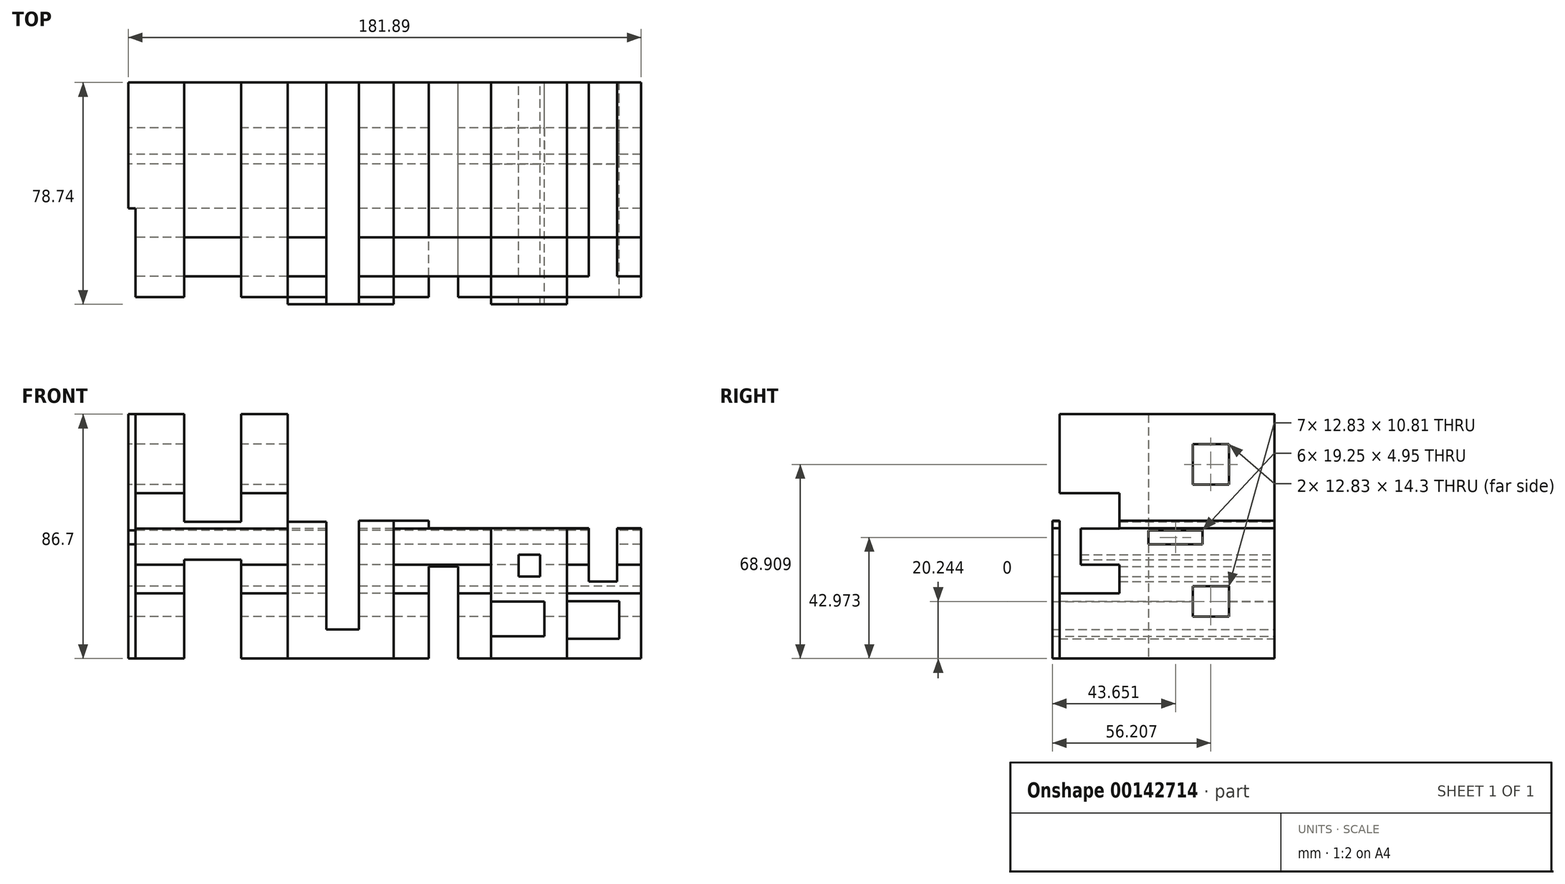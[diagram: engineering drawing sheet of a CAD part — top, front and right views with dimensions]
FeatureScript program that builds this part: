
annotation { "Feature Type Name" : "Feature", "Feature Type Description" : "" }
export const myFeature = defineFeature(function(context is Context, id is Id, definition is map)
    precondition{}
    {
        {
            var Q0;
            Q0=qCreatedBy(makeId("Front.planeOp"),FACE);
            var sketch = newSketch(context, id + "F0", { "sketchPlane" : qUnion([Q0])});
            skLineSegment(sketch, "E0.bottom", {"start": v(-93.93, -43.35) * mm, "end": v(-76.62, -43.35) * mm});
            skLineSegment(sketch, "E0.top", {"start": v(-93.93, 43.35) * mm, "end": v(-76.62, 43.35) * mm});
            skPoint(sketch, "E0.middle", {"position": v(0, 0) * mm});
            skLineSegment(sketch, "E1.right", {"start": v(-76.62, 43.35) * mm, "end": v(-76.62, 5.22) * mm});
            skLineSegment(sketch, "E2.bottom", {"start": v(-76.62, -8.34) * mm, "end": v(-56.46, -8.34) * mm});
            skLineSegment(sketch, "E2.top", {"start": v(-76.62, 5.22) * mm, "end": v(-56.46, 5.22) * mm});
            skLineSegment(sketch, "E3.top", {"start": v(-56.46, 43.35) * mm, "end": v(-39.96, 43.35) * mm});
            skLineSegment(sketch, "E3.left", {"start": v(-56.46, 5.22) * mm, "end": v(-56.46, 43.35) * mm});
            skLineSegment(sketch, "E3.right", {"start": v(-39.96, 5.22) * mm, "end": v(-39.96, 43.35) * mm});
            skLineSegment(sketch, "E4.left", {"start": v(-39.96, 5.22) * mm, "end": v(-39.96, 5.22) * mm});
            skLineSegment(sketch, "E4.right", {"start": v(-56.46, 5.22) * mm, "end": v(-56.46, 5.22) * mm});
            skLineSegment(sketch, "E5.top", {"start": v(-39.96, -43.35) * mm, "end": v(-56.46, -43.35) * mm});
            skLineSegment(sketch, "E5.left", {"start": v(-39.96, 5.22) * mm, "end": v(-39.96, -43.35) * mm});
            skLineSegment(sketch, "E5.right", {"start": v(-56.46, -8.34) * mm, "end": v(-56.46, -43.35) * mm});
            skLineSegment(sketch, "E6.bottom", {"start": v(-39.96, 5.22) * mm, "end": v(-26.21, 5.22) * mm});
            skLineSegment(sketch, "E6.right", {"start": v(-26.21, 5.22) * mm, "end": v(-26.21, -33.09) * mm});
            skLineSegment(sketch, "E7.bottom", {"start": v(-26.21, -43.35) * mm, "end": v(-14.66, -43.35) * mm});
            skLineSegment(sketch, "E7.top", {"start": v(-26.21, -33.09) * mm, "end": v(-14.66, -33.09) * mm});
            skLineSegment(sketch, "E8.bottom", {"start": v(-14.66, -43.35) * mm, "end": v(-2.38, -43.35) * mm});
            skLineSegment(sketch, "E8.top", {"start": v(-14.66, 5.6) * mm, "end": v(-2.38, 5.6) * mm});
            skLineSegment(sketch, "E8.left", {"start": v(-14.66, -33.09) * mm, "end": v(-14.66, 5.6) * mm});
            skLineSegment(sketch, "E8.right", {"start": v(-2.38, -43.35) * mm, "end": v(-2.38, 5.6) * mm});
            skLineSegment(sketch, "E9.trimOffspring", {"start": v(-76.62, -8.34) * mm, "end": v(-76.62, -43.35) * mm});
            skLineSegment(sketch, "E10.bottom", {"start": v(-2.38, 5.6) * mm, "end": v(10.08, 5.6) * mm});
            skLineSegment(sketch, "E10.top", {"start": v(-2.38, -43.35) * mm, "end": v(10.08, -43.35) * mm});
            skLineSegment(sketch, "E10.left", {"start": v(-2.38, 5.6) * mm, "end": v(-2.38, -43.35) * mm});
            skLineSegment(sketch, "E10.right", {"start": v(10.08, 5.6) * mm, "end": v(10.08, 2.84) * mm});
            skLineSegment(sketch, "E11.bottom", {"start": v(10.08, 2.84) * mm, "end": v(32.26, 2.84) * mm});
            skLineSegment(sketch, "E11.top", {"start": v(10.08, -10.72) * mm, "end": v(20.53, -10.72) * mm});
            skLineSegment(sketch, "E11.right", {"start": v(32.26, 2.84) * mm, "end": v(32.26, -10.72) * mm});
            skLineSegment(sketch, "E12.top", {"start": v(32.26, -43.35) * mm, "end": v(20.53, -43.35) * mm});
            skLineSegment(sketch, "E12.left", {"start": v(32.26, -10.72) * mm, "end": v(32.26, -43.35) * mm});
            skLineSegment(sketch, "E12.right", {"start": v(20.53, -10.72) * mm, "end": v(20.53, -43.35) * mm});
            skLineSegment(sketch, "E13.bottom", {"start": v(32.26, 2.84) * mm, "end": v(59.2, 2.84) * mm});
            skLineSegment(sketch, "E13.top", {"start": v(32.26, -23.19) * mm, "end": v(51.14, -23.19) * mm});
            skLineSegment(sketch, "E13.left", {"start": v(32.26, 2.84) * mm, "end": v(32.26, -23.19) * mm});
            skLineSegment(sketch, "E13.right", {"start": v(59.2, 2.84) * mm, "end": v(59.2, -23.19) * mm});
            skLineSegment(sketch, "E14.bottom", {"start": v(41.98, -6.5) * mm, "end": v(49.67, -6.5) * mm});
            skLineSegment(sketch, "E14.top", {"start": v(41.98, -14.2) * mm, "end": v(49.67, -14.2) * mm});
            skLineSegment(sketch, "E14.left", {"start": v(41.98, -6.5) * mm, "end": v(41.98, -14.2) * mm});
            skLineSegment(sketch, "E14.right", {"start": v(49.67, -6.5) * mm, "end": v(49.67, -14.2) * mm});
            skLineSegment(sketch, "E15.top", {"start": v(59.2, -43.35) * mm, "end": v(51.14, -43.35) * mm});
            skLineSegment(sketch, "E15.left", {"start": v(59.2, -23.19) * mm, "end": v(59.2, -43.35) * mm});
            skLineSegment(sketch, "E16.bottom", {"start": v(51.14, -43.35) * mm, "end": v(32.26, -43.35) * mm});
            skLineSegment(sketch, "E16.top", {"start": v(51.14, -35.47) * mm, "end": v(32.26, -35.47) * mm});
            skLineSegment(sketch, "E16.right", {"start": v(32.26, -43.35) * mm, "end": v(32.26, -35.47) * mm});
            skLineSegment(sketch, "E17", {"start": v(51.14, -35.47) * mm, "end": v(51.14, -23.19) * mm});
            skLineSegment(sketch, "E18.trimOffspring", {"start": v(10.08, -10.72) * mm, "end": v(10.08, -43.35) * mm});
            skLineSegment(sketch, "E19.bottom", {"start": v(59.2, 2.84) * mm, "end": v(66.9, 2.84) * mm});
            skLineSegment(sketch, "E19.top", {"start": v(59.2, -23) * mm, "end": v(77.72, -23) * mm});
            skLineSegment(sketch, "E19.left", {"start": v(59.2, 2.84) * mm, "end": v(59.2, -23) * mm});
            skLineSegment(sketch, "E19.right", {"start": v(85.42, 2.84) * mm, "end": v(85.42, -23) * mm});
            skLineSegment(sketch, "E20.top", {"start": v(66.9, -16.04) * mm, "end": v(76.99, -16.04) * mm});
            skLineSegment(sketch, "E20.left", {"start": v(66.9, 2.84) * mm, "end": v(66.9, -16.04) * mm});
            skLineSegment(sketch, "E20.right", {"start": v(76.99, 2.84) * mm, "end": v(76.99, -16.04) * mm});
            skLineSegment(sketch, "E21.top", {"start": v(85.42, -43.35) * mm, "end": v(77.72, -43.35) * mm});
            skLineSegment(sketch, "E21.left", {"start": v(85.42, -23) * mm, "end": v(85.42, -43.35) * mm});
            skLineSegment(sketch, "E21.right", {"start": v(77.72, -23) * mm, "end": v(77.72, -36.38) * mm});
            skLineSegment(sketch, "E22.bottom", {"start": v(77.72, -43.35) * mm, "end": v(59.2, -43.35) * mm});
            skLineSegment(sketch, "E22.top", {"start": v(77.72, -36.38) * mm, "end": v(59.2, -36.38) * mm});
            skLineSegment(sketch, "E22.right", {"start": v(59.2, -43.35) * mm, "end": v(59.2, -36.38) * mm});
            skLineSegment(sketch, "E23.trimOffspring", {"start": v(76.99, 2.84) * mm, "end": v(85.42, 2.84) * mm});
            skLineSegment(sketch, "E24.trimOffspring", {"start": v(-56.46, -43.35) * mm, "end": v(10.08, -43.35) * mm});
            skLineSegment(sketch, "E25.trimOffspring", {"start": v(20.53, -43.35) * mm, "end": v(85.42, -43.35) * mm});
            skPoint(sketch, "E0.right.end.orphan", {"position": v(101.55, 43.35) * mm});
            skPoint(sketch, "E0.right.start.orphan", {"position": v(101.55, -43.35) * mm});
            skLineSegment(sketch, "E26", {"start": v(-93.93, 43.35) * mm, "end": v(-93.93, -43.35) * mm});
            skPoint(sketch, "E0.left.end.orphan", {"position": v(-101.55, 43.35) * mm});
            skPoint(sketch, "E27.orphan", {"position": v(-101.55, -43.35) * mm});
            skSolve(sketch);
        }
        {
            var Q0;
            Q0=makeQuery(id+"F0.imprint","IMPRINT",FACE,{"disambiguationData":[TD([[makeQuery(id+"F0.imprint","IMPRINT",EDGE,{"derivedFrom":sQuery(id+"F0.wireOp",EDGE,"E0.top")}),-1.0]])]});
            var Q1;
            Q1=makeQuery(id+"F0.imprint","IMPRINT",FACE,{"disambiguationData":[TD([[makeQuery(id+"F0.imprint","IMPRINT",EDGE,{"derivedFrom":sQuery(id+"F0.wireOp",EDGE,"E10.bottom")}),-1.0]])]});
            var Q2;
            Q2=makeQuery(id+"F0.imprint","IMPRINT",FACE,{"disambiguationData":[TD([[makeQuery(id+"F0.imprint","IMPRINT",EDGE,{"derivedFrom":sQuery(id+"F0.wireOp",EDGE,"E19.bottom")}),-1.0]])]});
            extrude(context, id + "F1", {"entities" : qUnion([Q0, Q1, Q2]), "depth" : 76.2 * mm});
        }
        {
            var Q0;
            Q0=makeQuery(id+"F0.imprint","IMPRINT",FACE,{"disambiguationData":[TD([[makeQuery(id+"F0.imprint","IMPRINT",EDGE,{"derivedFrom":sQuery(id+"F0.wireOp",EDGE,"E6.bottom")}),-1.0]])]});
            var Q1;
            {var subQ1=sQuery(id+"F0.wireOp",EDGE,"E13.bottom");Q1=makeQuery(id+"F0.imprint","IMPRINT",FACE,{"disambiguationData":[TD([[makeQuery(id+"F0.imprint","IMPRINT",EDGE,{"derivedFrom":subQ1}),-1.0]])]});}
            extrude(context, id + "F2", {"entities" : qUnion([Q0, Q1]), "depth" : 78.74 * mm});
        }
        {
            var Q0;
            Q0=makeQuery(id+"F1.opExtrude","SWEPT_FACE",FACE,{"disambiguationData":[OSD([sQuery(id+"F0.wireOp",EDGE,"E26")])]});
            var sketch = newSketch(context, id + "F3", { "sketchPlane" : qUnion([Q0])});
            skLineSegment(sketch, "E28.bottom", {"start": v(0, 43.35) * mm, "end": v(44.71, 43.35) * mm});
            skLineSegment(sketch, "E28.top", {"start": v(0, -43.35) * mm, "end": v(44.71, -43.35) * mm});
            skLineSegment(sketch, "E28.left", {"start": v(0, 43.35) * mm, "end": v(0, -43.35) * mm});
            skLineSegment(sketch, "E28.right", {"start": v(44.71, 43.35) * mm, "end": v(44.71, 2.1) * mm});
            skLineSegment(sketch, "E29.bottom", {"start": v(16.12, -28.51) * mm, "end": v(28.95, -28.51) * mm});
            skLineSegment(sketch, "E29.top", {"start": v(16.12, 32.7) * mm, "end": v(28.95, 32.7) * mm});
            skLineSegment(sketch, "E29.left", {"start": v(16.12, -28.51) * mm, "end": v(16.12, -17.7) * mm});
            skLineSegment(sketch, "E29.right", {"start": v(28.95, -28.51) * mm, "end": v(28.95, -17.7) * mm});
            skPoint(sketch, "E30.oppositeSnap0", {"position": v(28.95, 2.1) * mm});
            skLineSegment(sketch, "E30.bottom", {"start": v(44.71, -2.85) * mm, "end": v(25.47, -2.85) * mm});
            skLineSegment(sketch, "E30.top", {"start": v(44.71, 2.1) * mm, "end": v(25.47, 2.1) * mm});
            skLineSegment(sketch, "E30.right", {"start": v(25.47, -2.85) * mm, "end": v(25.47, 2.1) * mm});
            skLineSegment(sketch, "E31", {"start": v(16.12, 18.41) * mm, "end": v(28.95, 18.41) * mm});
            skLineSegment(sketch, "E32", {"start": v(16.12, -17.7) * mm, "end": v(28.95, -17.7) * mm});
            skLineSegment(sketch, "E33.trimOffspring", {"start": v(16.12, 18.41) * mm, "end": v(16.12, 32.7) * mm});
            skLineSegment(sketch, "E34.trimOffspring", {"start": v(28.95, 18.41) * mm, "end": v(28.95, 32.7) * mm});
            skLineSegment(sketch, "E35.trimOffspring", {"start": v(44.71, -2.85) * mm, "end": v(44.71, -43.35) * mm});
            skLineSegment(sketch, "E36.bottom", {"start": v(44.71, 43.35) * mm, "end": v(54.98, 43.35) * mm});
            skLineSegment(sketch, "E36.top", {"start": v(44.71, -43.35) * mm, "end": v(54.98, -43.35) * mm});
            skLineSegment(sketch, "E36.right", {"start": v(54.98, 15.3) * mm, "end": v(54.98, 2.83) * mm});
            skLineSegment(sketch, "E37.bottom", {"start": v(54.98, 43.35) * mm, "end": v(76.2, 43.35) * mm});
            skLineSegment(sketch, "E37.top", {"start": v(54.98, 15.3) * mm, "end": v(76.2, 15.3) * mm});
            skLineSegment(sketch, "E37.right", {"start": v(76.2, 43.35) * mm, "end": v(76.2, 15.3) * mm});
            skLineSegment(sketch, "E38.bottom", {"start": v(54.98, 2.83) * mm, "end": v(68.72, 2.83) * mm});
            skLineSegment(sketch, "E38.top", {"start": v(54.98, -10) * mm, "end": v(68.72, -10) * mm});
            skLineSegment(sketch, "E38.right", {"start": v(68.72, 2.83) * mm, "end": v(68.72, -10) * mm});
            skLineSegment(sketch, "E39.bottom", {"start": v(54.98, -20.27) * mm, "end": v(76.2, -20.27) * mm});
            skLineSegment(sketch, "E39.top", {"start": v(54.98, -43.35) * mm, "end": v(76.2, -43.35) * mm});
            skLineSegment(sketch, "E39.right", {"start": v(76.2, -20.27) * mm, "end": v(76.2, -43.35) * mm});
            skLineSegment(sketch, "E40.trimOffspring", {"start": v(54.98, -10) * mm, "end": v(54.98, -20.27) * mm});
            skLineSegment(sketch, "E41", {"start": v(44.71, -2.85) * mm, "end": v(44.71, 2.1) * mm});
            skSolve(sketch);
        }
        {
            var Q0;
            Q0=makeQuery(id+"F3.imprint","IMPRINT",FACE,{"disambiguationData":[TD([[makeQuery(id+"F3.imprint","IMPRINT",EDGE,{"derivedFrom":sQuery(id+"F3.wireOp",EDGE,"E30.bottom")}),-1.0]])]});
            var Q1;
            Q1=makeQuery(id+"F3.imprint","IMPRINT",FACE,{"disambiguationData":[TD([[makeQuery(id+"F3.imprint","IMPRINT",EDGE,{"derivedFrom":sQuery(id+"F3.wireOp",EDGE,"E36.right")}),1.0]])]});
            var Q2;
            Q2=makeQuery(id+"F3.imprint","IMPRINT",FACE,{"disambiguationData":[TD([[makeQuery(id+"F3.imprint","IMPRINT",EDGE,{"derivedFrom":sQuery(id+"F3.wireOp",EDGE,"E29.top")}),-1.0]])]});
            var Q3;
            Q3=makeQuery(id+"F3.imprint","IMPRINT",FACE,{"disambiguationData":[TD([[makeQuery(id+"F3.imprint","IMPRINT",EDGE,{"derivedFrom":sQuery(id+"F3.wireOp",EDGE,"E29.bottom")}),1.0]])]});
            extrude(context, id + "F4", {"entities" : qUnion([Q0, Q1, Q2, Q3]), "operationType" : NewBodyOperationType.REMOVE, "endBound" : BoundingType.THROUGH_ALL, "oppositeDirection" : true, "depth" : 25.4 * mm});
        }
        {
            var Q0;
            Q0=makeQuery(id+"F3.imprint","IMPRINT",FACE,{"disambiguationData":[TD([[makeQuery(id+"F3.imprint","IMPRINT",EDGE,{"derivedFrom":sQuery(id+"F3.wireOp",EDGE,"E28.bottom")}),1.0]])]});
            extrude(context, id + "F5", {"entities" : qUnion([Q0]), "operationType" : NewBodyOperationType.ADD, "depth" : 2.54 * mm});
        }
    });
